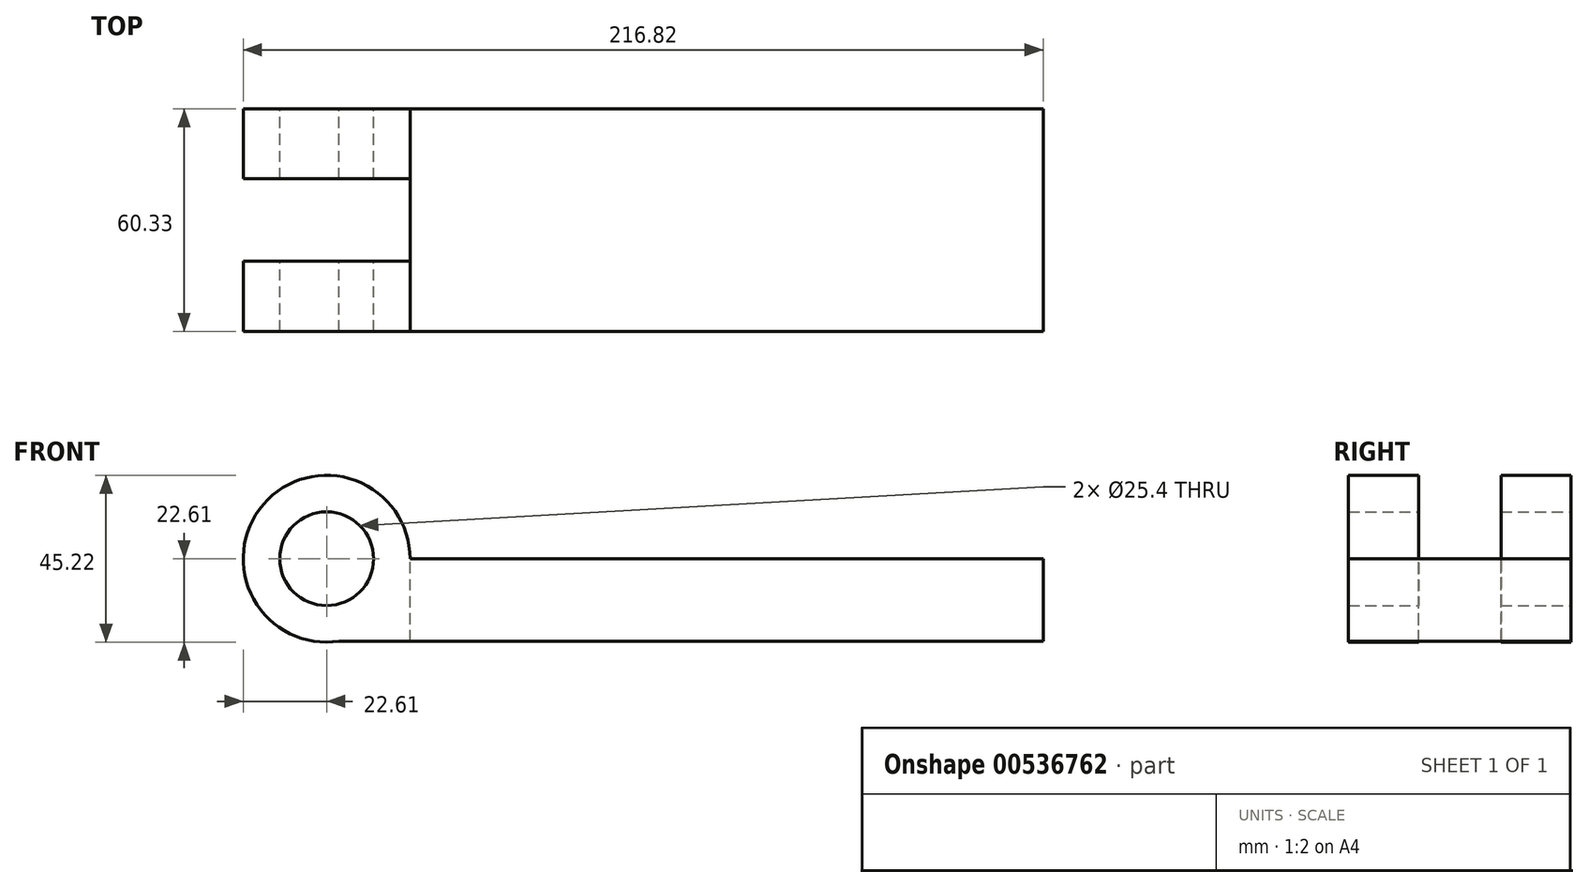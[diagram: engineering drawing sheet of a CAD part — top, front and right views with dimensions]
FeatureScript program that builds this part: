
annotation { "Feature Type Name" : "Feature", "Feature Type Description" : "" }
export const myFeature = defineFeature(function(context is Context, id is Id, definition is map)
    precondition{}
    {
        {
            var Q0;
            Q0=qCreatedBy(makeId("Front.planeOp"),FACE);
            var sketch = newSketch(context, id + "F0", { "sketchPlane" : qUnion([Q0])});
            skCircle(sketch, "E0", {"center": v(0, 0) * mm, "radius": 12.7 * mm});
            skCircle(sketch, "E1", {"center": v(0, 0) * mm, "radius": 22.6 * mm});
            skLineSegment(sketch, "E2.bottom", {"start": v(0, 0) * mm, "end": v(194.2, 0) * mm});
            skLineSegment(sketch, "E2.top", {"start": v(0, -22.35) * mm, "end": v(194.2, -22.35) * mm});
            skLineSegment(sketch, "E2.left", {"start": v(0, 0) * mm, "end": v(0, -22.35) * mm});
            skLineSegment(sketch, "E2.right", {"start": v(194.2, 0) * mm, "end": v(194.2, -22.35) * mm});
            skSolve(sketch);
        }
        {
            var Q0;
            Q0 = qSketchRegion(id + "F0", true);
            extrude(context, id + "F1", {"entities" : qUnion([Q0]), "depth" : 60.32 * mm, "offsetDistance" : 25.4 * mm});
        }
        {
            var Q0;
            Q0=qCreatedBy(makeId("Top.planeOp"),FACE);
            var sketch = newSketch(context, id + "F2", { "sketchPlane" : qUnion([Q0])});
            skLineSegment(sketch, "E3", {"start": v(-22.6, -60.33) * mm, "end": v(-22.6, 0) * mm});
            skLineSegment(sketch, "E4", {"start": v(-22.6, -19) * mm, "end": v(22.6, -19) * mm});
            skLineSegment(sketch, "E5", {"start": v(22.6, -19) * mm, "end": v(22.6, -41.33) * mm});
            skLineSegment(sketch, "E6", {"start": v(22.6, -41.33) * mm, "end": v(-22.6, -41.33) * mm});
            skSolve(sketch);
        }
        {
            var Q0;
            Q0 = qSketchRegion(id + "F2", true);
            extrude(context, id + "F3", {"entities" : qUnion([Q0]), "operationType" : NewBodyOperationType.REMOVE, "endBound" : BoundingType.THROUGH_ALL, "oppositeDirection" : true, "depth" : 25.4 * mm, "offsetDistance" : 25.4 * mm, "hasSecondDirection" : true, "secondDirectionBound" : SecondDirectionBoundingType.THROUGH_ALL, "secondDirectionOppositeDirection" : false, "secondDirectionDepth" : 25.4 * mm});
        }
    });
